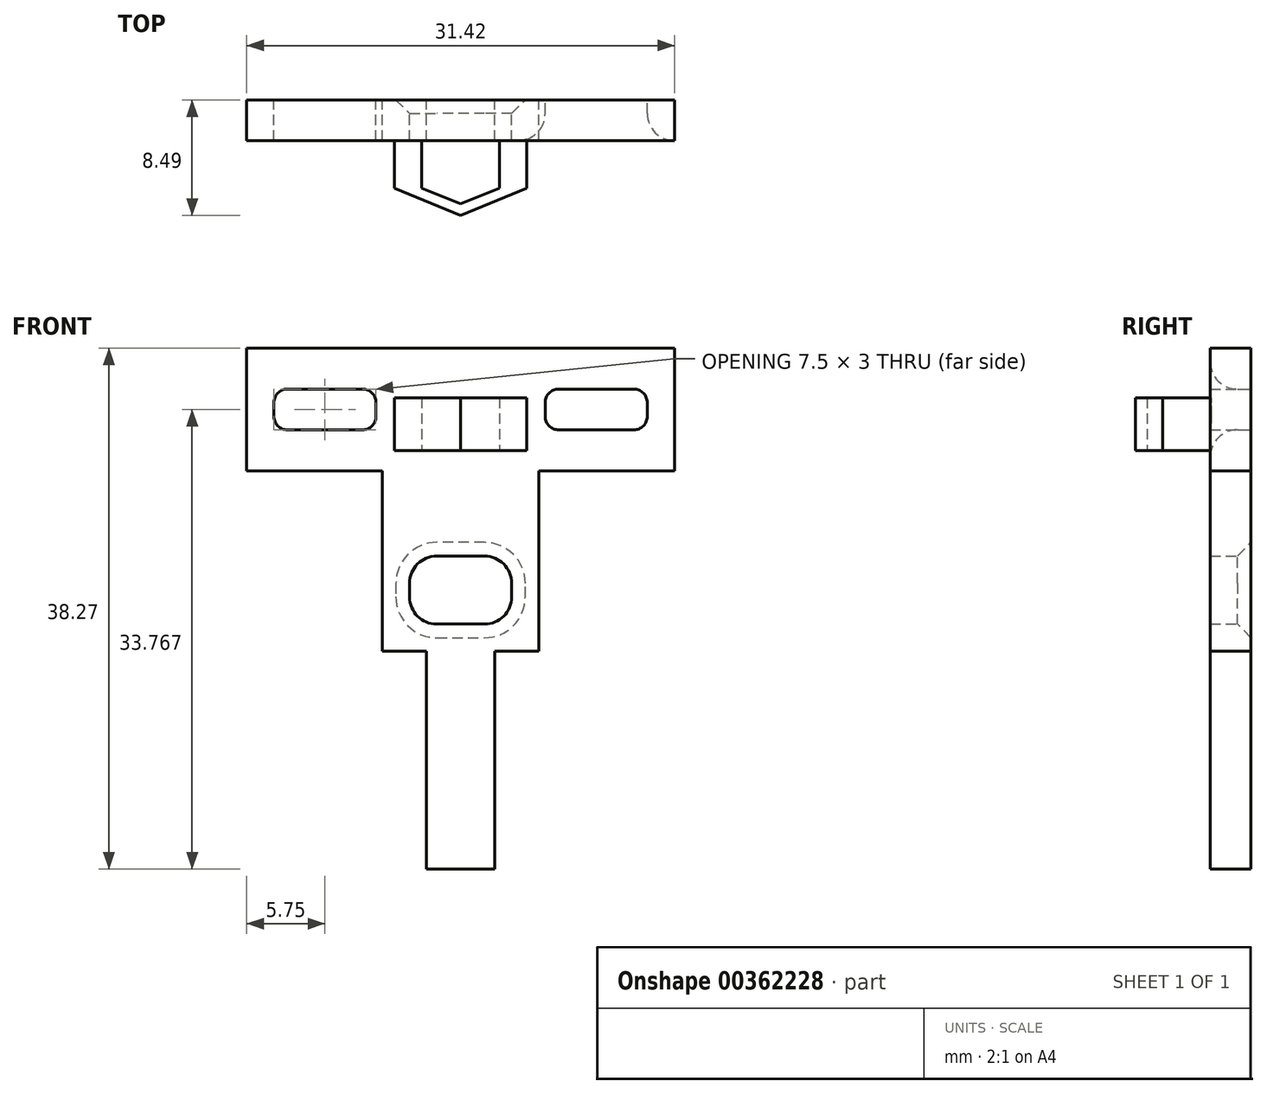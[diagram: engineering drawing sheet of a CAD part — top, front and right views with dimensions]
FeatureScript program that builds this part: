
annotation { "Feature Type Name" : "Feature", "Feature Type Description" : "" }
export const myFeature = defineFeature(function(context is Context, id is Id, definition is map)
    precondition{}
    {
        {
            var Q0;
            Q0=qCreatedBy(makeId("Front.planeOp"),FACE);
            var sketch = newSketch(context, id + "F0", { "sketchPlane" : qUnion([Q0])});
            skLineSegment(sketch, "E0", {"start": v(-3.75, 0) * mm, "end": v(3.75, 0) * mm, "construction": true});
            skPoint(sketch, "E1", {"position": v(0, 0) * mm});
            skPoint(sketch, "E2", {"position": v(-5.75, 0) * mm});
            skPoint(sketch, "E3", {"position": v(5.75, 0) * mm});
            skLineSegment(sketch, "E4.bottom", {"start": v(-1.75, 2.5) * mm, "end": v(1.75, 2.5) * mm});
            skLineSegment(sketch, "E4.top", {"start": v(-1.75, -2.5) * mm, "end": v(1.75, -2.5) * mm});
            skLineSegment(sketch, "E4.left", {"start": v(-3.75, 0.5) * mm, "end": v(-3.75, -0.5) * mm});
            skLineSegment(sketch, "E4.right", {"start": v(3.75, 0.5) * mm, "end": v(3.75, -0.5) * mm});
            skPoint(sketch, "E5.visualSharp", {"position": v(-3.75, 2.5) * mm});
            skArc(sketch, "E5.filletArc", {"start": v(-1.75, 2.5) * mm, "mid": v(-3.16, 1.91) * mm, "end": v(-3.75, 0.5) * mm});
            skPoint(sketch, "E6.visualSharp", {"position": v(3.75, 2.5) * mm});
            skArc(sketch, "E6.filletArc", {"start": v(3.75, 0.5) * mm, "mid": v(3.16, 1.91) * mm, "end": v(1.75, 2.5) * mm});
            skPoint(sketch, "E7.visualSharp", {"position": v(3.75, -2.5) * mm});
            skArc(sketch, "E7.filletArc", {"start": v(1.75, -2.5) * mm, "mid": v(3.16, -1.91) * mm, "end": v(3.75, -0.5) * mm});
            skPoint(sketch, "E8.visualSharp", {"position": v(-3.75, -2.5) * mm});
            skArc(sketch, "E8.filletArc", {"start": v(-3.75, -0.5) * mm, "mid": v(-3.16, -1.91) * mm, "end": v(-1.75, -2.5) * mm});
            skLineSegment(sketch, "E9", {"start": v(-5.75, 17.77) * mm, "end": v(15.71, 17.77) * mm});
            skPoint(sketch, "E10", {"position": v(0, 17.77) * mm});
            skLineSegment(sketch, "E11", {"start": v(-6.21, 13.27) * mm, "end": v(-13.71, 13.27) * mm, "construction": true});
            skLineSegment(sketch, "E12.bottom", {"start": v(-7.21, 14.77) * mm, "end": v(-12.71, 14.77) * mm});
            skLineSegment(sketch, "E12.top", {"start": v(-7.21, 11.77) * mm, "end": v(-12.71, 11.77) * mm});
            skLineSegment(sketch, "E12.left", {"start": v(-6.21, 13.77) * mm, "end": v(-6.21, 12.77) * mm});
            skLineSegment(sketch, "E12.right", {"start": v(-13.71, 13.77) * mm, "end": v(-13.71, 12.77) * mm});
            skPoint(sketch, "E12.middle", {"position": v(-9.96, 13.27) * mm});
            skPoint(sketch, "E13.visualSharp", {"position": v(-6.21, 11.77) * mm});
            skArc(sketch, "E13.filletArc", {"start": v(-7.21, 11.77) * mm, "mid": v(-6.5, 12.06) * mm, "end": v(-6.21, 12.77) * mm});
            skPoint(sketch, "E14.visualSharp", {"position": v(-6.21, 14.77) * mm});
            skArc(sketch, "E14.filletArc", {"start": v(-6.21, 13.77) * mm, "mid": v(-6.5, 14.47) * mm, "end": v(-7.21, 14.77) * mm});
            skPoint(sketch, "E15.visualSharp", {"position": v(-13.71, 14.77) * mm});
            skArc(sketch, "E15.filletArc", {"start": v(-12.71, 14.77) * mm, "mid": v(-13.42, 14.47) * mm, "end": v(-13.71, 13.77) * mm});
            skPoint(sketch, "E16.visualSharp", {"position": v(-13.71, 11.77) * mm});
            skArc(sketch, "E16.filletArc", {"start": v(-13.71, 12.77) * mm, "mid": v(-13.42, 12.06) * mm, "end": v(-12.71, 11.77) * mm});
            skLineSegment(sketch, "E17", {"start": v(-15.71, 17.77) * mm, "end": v(-15.71, 8.77) * mm});
            skLineSegment(sketch, "E18", {"start": v(-15.71, 8.77) * mm, "end": v(-5.75, 8.77) * mm});
            skLineSegment(sketch, "E19.trimOffspring", {"start": v(-5.75, 8.77) * mm, "end": v(-5.75, -4.5) * mm});
            skPoint(sketch, "E20", {"position": v(-15.71, 13.27) * mm});
            skLineSegment(sketch, "E21.MirrorCS", {"start": v(-13.71, 12.77) * mm, "end": v(-13.71, 13.77) * mm});
            skLineSegment(sketch, "E22.MirrorCS", {"start": v(-6.21, 12.77) * mm, "end": v(-6.21, 13.77) * mm});
            skArc(sketch, "E23.MirrorCS", {"start": v(-6.21, 12.77) * mm, "mid": v(-6.5, 12.06) * mm, "end": v(-7.21, 11.77) * mm});
            skArc(sketch, "E24.MirrorCS", {"start": v(-13.71, 13.77) * mm, "mid": v(-13.42, 14.47) * mm, "end": v(-12.71, 14.77) * mm});
            skArc(sketch, "E25.MirrorCS", {"start": v(-12.71, 11.77) * mm, "mid": v(-13.42, 12.06) * mm, "end": v(-13.71, 12.77) * mm});
            skArc(sketch, "E26.MirrorCS", {"start": v(-7.21, 14.77) * mm, "mid": v(-6.5, 14.47) * mm, "end": v(-6.21, 13.77) * mm});
            skLineSegment(sketch, "E27.MirrorCS", {"start": v(-15.71, 8.77) * mm, "end": v(-15.71, 17.77) * mm});
            skLineSegment(sketch, "E28.MirrorCS", {"start": v(-15.71, 17.77) * mm, "end": v(-5.75, 17.77) * mm});
            skLineSegment(sketch, "E29.MirrorCS", {"start": v(6.21, 12.77) * mm, "end": v(6.21, 13.77) * mm});
            skLineSegment(sketch, "E30.MirrorCS", {"start": v(13.71, 13.77) * mm, "end": v(13.71, 12.77) * mm});
            skLineSegment(sketch, "E31.MirrorCS", {"start": v(6.21, 13.77) * mm, "end": v(6.21, 12.77) * mm});
            skLineSegment(sketch, "E32.MirrorCS", {"start": v(13.71, 12.77) * mm, "end": v(13.71, 13.77) * mm});
            skArc(sketch, "E33.MirrorCS", {"start": v(7.21, 11.77) * mm, "mid": v(6.5, 12.06) * mm, "end": v(6.21, 12.77) * mm});
            skArc(sketch, "E34.MirrorCS", {"start": v(13.71, 12.77) * mm, "mid": v(13.42, 12.06) * mm, "end": v(12.71, 11.77) * mm});
            skArc(sketch, "E35.MirrorCS", {"start": v(6.21, 13.77) * mm, "mid": v(6.5, 14.47) * mm, "end": v(7.21, 14.77) * mm});
            skArc(sketch, "E36.MirrorCS", {"start": v(12.71, 14.77) * mm, "mid": v(13.42, 14.47) * mm, "end": v(13.71, 13.77) * mm});
            skArc(sketch, "E37.MirrorCS", {"start": v(6.21, 12.77) * mm, "mid": v(6.5, 12.06) * mm, "end": v(7.21, 11.77) * mm});
            skArc(sketch, "E38.MirrorCS", {"start": v(7.21, 14.77) * mm, "mid": v(6.5, 14.47) * mm, "end": v(6.21, 13.77) * mm});
            skArc(sketch, "E39.MirrorCS", {"start": v(12.71, 11.77) * mm, "mid": v(13.42, 12.06) * mm, "end": v(13.71, 12.77) * mm});
            skArc(sketch, "E40.MirrorCS", {"start": v(13.71, 13.77) * mm, "mid": v(13.42, 14.47) * mm, "end": v(12.71, 14.77) * mm});
            skPoint(sketch, "E41.MirrorP", {"position": v(9.96, 13.27) * mm});
            skPoint(sketch, "E42.MirrorP", {"position": v(6.21, 11.77) * mm});
            skPoint(sketch, "E43.MirrorP", {"position": v(13.71, 14.77) * mm});
            skPoint(sketch, "E44.MirrorP", {"position": v(6.21, 14.77) * mm});
            skLineSegment(sketch, "E45.MirrorCS", {"start": v(15.71, 17.77) * mm, "end": v(15.71, 8.77) * mm});
            skPoint(sketch, "E46.MirrorP", {"position": v(13.71, 11.77) * mm});
            skLineSegment(sketch, "E47.MirrorCS", {"start": v(7.21, 14.77) * mm, "end": v(12.71, 14.77) * mm});
            skLineSegment(sketch, "E48.MirrorCS", {"start": v(7.21, 11.77) * mm, "end": v(12.71, 11.77) * mm});
            skLineSegment(sketch, "E49.MirrorCS", {"start": v(15.71, 8.77) * mm, "end": v(15.71, 17.77) * mm});
            skPoint(sketch, "E50.MirrorP", {"position": v(15.71, 13.27) * mm});
            skLineSegment(sketch, "E51.MirrorCS", {"start": v(15.71, 15.66) * mm, "end": v(15.71, 6.66) * mm});
            skLineSegment(sketch, "E52.MirrorCS", {"start": v(6.21, 13.27) * mm, "end": v(13.71, 13.27) * mm, "construction": true});
            skLineSegment(sketch, "E53.MirrorCS", {"start": v(15.71, 8.77) * mm, "end": v(5.75, 8.77) * mm});
            skLineSegment(sketch, "E54.MirrorCS", {"start": v(5.75, 8.77) * mm, "end": v(5.75, -4.5) * mm});
            skLineSegment(sketch, "E55", {"start": v(-5.75, -4.5) * mm, "end": v(-2.5, -4.5) * mm});
            skPoint(sketch, "E56.orphan", {"position": v(-5.75, -12.65) * mm});
            skPoint(sketch, "E57.orphan", {"position": v(5.75, -12.65) * mm});
            skLineSegment(sketch, "E58", {"start": v(0, -4.5) * mm, "end": v(0, -20.5) * mm, "construction": true});
            skLineSegment(sketch, "E59.top", {"start": v(-2.5, -20.5) * mm, "end": v(2.5, -20.5) * mm});
            skLineSegment(sketch, "E59.left", {"start": v(-2.5, -4.5) * mm, "end": v(-2.5, -20.5) * mm});
            skLineSegment(sketch, "E59.right", {"start": v(2.5, -4.5) * mm, "end": v(2.5, -20.5) * mm});
            skPoint(sketch, "E59.middle", {"position": v(0, -12.5) * mm});
            skLineSegment(sketch, "E60.trimOffspring", {"start": v(2.5, -4.5) * mm, "end": v(5.75, -4.5) * mm});
            skPoint(sketch, "E61.MirrorCS.end.orphan", {"position": v(-5.75, 17.77) * mm});
            skLineSegment(sketch, "E62", {"start": v(-2.5, 10.58) * mm, "end": v(-2.5, 13.77) * mm, "construction": true});
            skLineSegment(sketch, "E63", {"start": v(-2.5, 13.77) * mm, "end": v(2.5, 13.77) * mm, "construction": true});
            skLineSegment(sketch, "E64", {"start": v(2.5, 13.77) * mm, "end": v(2.5, 10.58) * mm, "construction": true});
            skLineSegment(sketch, "E65", {"start": v(2.5, 10.58) * mm, "end": v(-2.5, 10.58) * mm, "construction": true});
            skLineSegment(sketch, "E66.0", {"start": v(2.85, 10.23) * mm, "end": v(-2.85, 10.23) * mm, "construction": true});
            skLineSegment(sketch, "E66.1", {"start": v(2.85, 14.12) * mm, "end": v(2.85, 10.23) * mm, "construction": true});
            skLineSegment(sketch, "E66.2", {"start": v(-2.85, 14.12) * mm, "end": v(2.85, 14.12) * mm, "construction": true});
            skLineSegment(sketch, "E66.3", {"start": v(-2.85, 10.23) * mm, "end": v(-2.85, 14.12) * mm, "construction": true});
            skLineSegment(sketch, "E67.bottom", {"start": v(-2.85, 14.12) * mm, "end": v(-4.85, 14.12) * mm});
            skLineSegment(sketch, "E67.top", {"start": v(-2.85, 10.23) * mm, "end": v(-4.85, 10.23) * mm});
            skLineSegment(sketch, "E67.left", {"start": v(-2.85, 14.12) * mm, "end": v(-2.85, 10.23) * mm});
            skLineSegment(sketch, "E67.right", {"start": v(-4.85, 14.12) * mm, "end": v(-4.85, 10.23) * mm});
            skLineSegment(sketch, "E68.bottom", {"start": v(2.85, 14.12) * mm, "end": v(4.85, 14.12) * mm});
            skLineSegment(sketch, "E68.top", {"start": v(2.85, 10.23) * mm, "end": v(4.85, 10.23) * mm});
            skLineSegment(sketch, "E68.left", {"start": v(2.85, 14.12) * mm, "end": v(2.85, 10.23) * mm});
            skLineSegment(sketch, "E68.right", {"start": v(4.85, 14.12) * mm, "end": v(4.85, 10.23) * mm});
            skSolve(sketch);
        }
        {
            var Q0;
            Q0=makeQuery(id+"F0.imprint","IMPRINT",FACE,{"disambiguationData":[TD([[makeQuery(id+"F0.imprint","IMPRINT",EDGE,{"derivedFrom":sQuery(id+"F0.wireOp",EDGE,"E4.bottom")}),1.0]])]});
            extrude(context, id + "F1", {"entities" : qUnion([Q0]), "depth" : 3 * mm});
        }
        {
            var Q0;
            Q0=makeQuery(id+"F0.imprint","IMPRINT",FACE,{"disambiguationData":[TD([[makeQuery(id+"F0.imprint","IMPRINT",EDGE,{"derivedFrom":sQuery(id+"F0.wireOp",EDGE,"E67.bottom")}),1.0]])]});
            var Q1;
            Q1=makeQuery(id+"F0.imprint","IMPRINT",FACE,{"disambiguationData":[TD([[makeQuery(id+"F0.imprint","IMPRINT",EDGE,{"derivedFrom":sQuery(id+"F0.wireOp",EDGE,"E68.bottom")}),-1.0]])]});
            var Q2;
            Q2=makeQuery(id+"F1.opExtrude","CAP_FACE",FACE,{"disambiguationData":[OSD([sQuery(id+"F0.wireOp",EDGE,"E4.bottom"),sQuery(id+"F0.wireOp",EDGE,"E4.top"),sQuery(id+"F0.wireOp",EDGE,"E4.left"),sQuery(id+"F0.wireOp",EDGE,"E4.right"),sQuery(id+"F0.wireOp",EDGE,"E5.filletArc"),sQuery(id+"F0.wireOp",EDGE,"E6.filletArc"),sQuery(id+"F0.wireOp",EDGE,"E7.filletArc"),sQuery(id+"F0.wireOp",EDGE,"E8.filletArc"),sQuery(id+"F0.wireOp",EDGE,"E9"),sQuery(id+"F0.wireOp",EDGE,"E18"),sQuery(id+"F0.wireOp",EDGE,"E19.trimOffspring"),sQuery(id+"F0.wireOp",EDGE,"E28.MirrorCS"),sQuery(id+"F0.wireOp",EDGE,"E12.left"),sQuery(id+"F0.wireOp",EDGE,"E12.right"),sQuery(id+"F0.wireOp",EDGE,"E23.MirrorCS"),sQuery(id+"F0.wireOp",EDGE,"E24.MirrorCS"),sQuery(id+"F0.wireOp",EDGE,"E16.filletArc"),sQuery(id+"F0.wireOp",EDGE,"E14.filletArc"),sQuery(id+"F0.wireOp",EDGE,"E12.bottom"),sQuery(id+"F0.wireOp",EDGE,"E27.MirrorCS"),sQuery(id+"F0.wireOp",EDGE,"E12.top"),sQuery(id+"F0.wireOp",EDGE,"E29.MirrorCS"),sQuery(id+"F0.wireOp",EDGE,"E32.MirrorCS"),sQuery(id+"F0.wireOp",EDGE,"E39.MirrorCS"),sQuery(id+"F0.wireOp",EDGE,"E40.MirrorCS"),sQuery(id+"F0.wireOp",EDGE,"E38.MirrorCS"),sQuery(id+"F0.wireOp",EDGE,"E37.MirrorCS"),sQuery(id+"F0.wireOp",EDGE,"E48.MirrorCS"),sQuery(id+"F0.wireOp",EDGE,"E51.MirrorCS"),sQuery(id+"F0.wireOp",EDGE,"E47.MirrorCS"),sQuery(id+"F0.wireOp",EDGE,"E53.MirrorCS"),sQuery(id+"F0.wireOp",EDGE,"E54.MirrorCS"),sQuery(id+"F0.wireOp",EDGE,"E55"),sQuery(id+"F0.wireOp",EDGE,"E59.top"),sQuery(id+"F0.wireOp",EDGE,"E59.left"),sQuery(id+"F0.wireOp",EDGE,"E59.right"),sQuery(id+"F0.wireOp",EDGE,"E60.trimOffspring"),sQuery(id+"F0.wireOp",EDGE,"E67.bottom"),sQuery(id+"F0.wireOp",EDGE,"E67.top"),sQuery(id+"F0.wireOp",EDGE,"E67.left"),sQuery(id+"F0.wireOp",EDGE,"E67.right"),sQuery(id+"F0.wireOp",EDGE,"E68.bottom"),sQuery(id+"F0.wireOp",EDGE,"E68.top"),sQuery(id+"F0.wireOp",EDGE,"E68.left"),sQuery(id+"F0.wireOp",EDGE,"E68.right")])],"isStart":false});
            extrude(context, id + "F2", {"entities" : qUnion([Q0, Q1]), "endBound" : BoundingType.UP_TO_SURFACE, "endBoundEntityFace" : qUnion([Q2]), "depth" : 25 * mm});
        }
        {
            var Q0;
            {Q0=qUnion([makeQuery(id+"F2.opExtrude","CAP_FACE",FACE,{"disambiguationData":[OSD([sQuery(id+"F0.wireOp",EDGE,"E67.bottom"),sQuery(id+"F0.wireOp",EDGE,"E67.top"),sQuery(id+"F0.wireOp",EDGE,"E67.left"),sQuery(id+"F0.wireOp",EDGE,"E67.right")])],"isStart":false}),makeQuery(id+"F2.opExtrude","CAP_FACE",FACE,{"disambiguationData":[OSD([sQuery(id+"F0.wireOp",EDGE,"E68.bottom"),sQuery(id+"F0.wireOp",EDGE,"E68.top"),sQuery(id+"F0.wireOp",EDGE,"E68.left"),sQuery(id+"F0.wireOp",EDGE,"E68.right")])],"isStart":false})]);}
            var Q1;
            {Q1=qUnion([makeQuery(id+"F2.opExtrude","CAP_FACE",FACE,{"disambiguationData":[OSD([sQuery(id+"F0.wireOp",EDGE,"E67.bottom"),sQuery(id+"F0.wireOp",EDGE,"E67.top"),sQuery(id+"F0.wireOp",EDGE,"E67.left"),sQuery(id+"F0.wireOp",EDGE,"E67.right")])],"isStart":false}),makeQuery(id+"F2.opExtrude","CAP_FACE",FACE,{"disambiguationData":[OSD([sQuery(id+"F0.wireOp",EDGE,"E68.bottom"),sQuery(id+"F0.wireOp",EDGE,"E68.top"),sQuery(id+"F0.wireOp",EDGE,"E68.left"),sQuery(id+"F0.wireOp",EDGE,"E68.right")])],"isStart":false})]);}
            extrude(context, id + "F3", {"entities" : qUnion([Q0, Q1]), "operationType" : NewBodyOperationType.ADD, "depth" : 3.5 * mm});
        }
        {
            var Q0;
            {var subQ0=sQuery(id+"F0.wireOp",EDGE,"E67.top");Q0=makeQuery(id+"F3.boolean.opBoolean","MERGE",FACE,{"derivedFrom":[makeQuery(id+"F2.opExtrude","SWEPT_FACE",FACE,{"disambiguationData":[OSD([subQ0])]}),makeQuery(id+"F3.opExtrude","SWEPT_FACE",FACE,{"disambiguationData":[OSD([subQ0])]})]});}
            var sketch = newSketch(context, id + "F4", { "sketchPlane" : qUnion([Q0])});
            skLineSegment(sketch, "E69.0", {"start": v(-2.85, 6.5) * mm, "end": v(-4.85, 6.5) * mm});
            skLineSegment(sketch, "E70.0", {"start": v(2.85, 6.5) * mm, "end": v(4.85, 6.5) * mm});
            skLineSegment(sketch, "E71", {"start": v(2.85, 6.5) * mm, "end": v(0, 7.63) * mm});
            skLineSegment(sketch, "E72", {"start": v(0, 7.63) * mm, "end": v(-2.85, 6.5) * mm});
            skLineSegment(sketch, "E73", {"start": v(-4.85, 6.5) * mm, "end": v(0, 8.49) * mm});
            skLineSegment(sketch, "E74", {"start": v(0, 8.49) * mm, "end": v(4.85, 6.5) * mm});
            skSolve(sketch);
        }
        {
            var Q0;
            Q0 = qSketchRegion(id + "F4", true);
            var Q1;
            {var subQ0=sQuery(id+"F0.wireOp",EDGE,"E67.bottom");Q1=makeQuery(id+"F3.boolean.opBoolean","MERGE",FACE,{"derivedFrom":[makeQuery(id+"F2.opExtrude","SWEPT_FACE",FACE,{"disambiguationData":[OSD([subQ0])]}),makeQuery(id+"F3.opExtrude","SWEPT_FACE",FACE,{"disambiguationData":[OSD([subQ0])]})]});}
            extrude(context, id + "F5", {"entities" : qUnion([Q0]), "operationType" : NewBodyOperationType.ADD, "endBound" : BoundingType.UP_TO_SURFACE, "oppositeDirection" : true, "endBoundEntityFace" : qUnion([Q1]), "depth" : 25 * mm});
        }
        {
            var Q0;
            Q0=makeQuery(id+"F1.opExtrude","CAP_EDGE",EDGE,{"disambiguationData":[OSD([sQuery(id+"F0.wireOp",EDGE,"E12.top")])],"isStart":false});
            var Q1;
            Q1=makeQuery(id+"F1.opExtrude","CAP_EDGE",EDGE,{"disambiguationData":[OSD([sQuery(id+"F0.wireOp",EDGE,"E48.MirrorCS")])],"isStart":false});
            fillet(context, id + "F6", {"entities" : qUnion([Q0, Q1]), "radius" : 2 * mm, "tangentPropagation" : true, "allowEdgeOverflow" : false});
        }
        {
            var Q0;
            Q0=makeQuery(id+"F1.opExtrude","CAP_EDGE",EDGE,{"disambiguationData":[OSD([sQuery(id+"F0.wireOp",EDGE,"E12.top")])],"isStart":true});
            var Q1;
            Q1=makeQuery(id+"F1.opExtrude","CAP_EDGE",EDGE,{"disambiguationData":[OSD([sQuery(id+"F0.wireOp",EDGE,"E38.MirrorCS")])],"isStart":true});
            var Q2;
            Q2=makeQuery(id+"F1.opExtrude","CAP_EDGE",EDGE,{"disambiguationData":[OSD([sQuery(id+"F0.wireOp",EDGE,"E4.bottom")])],"isStart":true});
            chamfer(context, id + "F7", {"entities" : qUnion([Q0, Q1, Q2]), "width" : 1 * mm, "tangentPropagation" : true});
        }
    });
